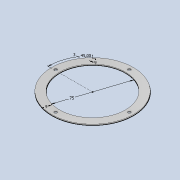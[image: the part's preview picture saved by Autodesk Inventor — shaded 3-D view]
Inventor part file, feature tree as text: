
AUTODESK INVENTOR PART (.ipt)
format: ipt  version: 2020.3 (Build 243373010, 373A)  size: 136,704 bytes
history: native  units: mm
features: sketch x2, extrude x2, hole x1, pattern_circular x1
ambient origin geometry x8: Origin, YZ Plane, XZ Plane, XY Plane, X Axis, Y Axis, Z Axis, Center Point
bodies: Solid1 (feature_tree)
feature tree (6):
  sketch  "Sketch2"  dims[d14=75.0mm d15=9.0mm]
  extrude  "Extrusion1"  Depth=9.0mm
  hole  "Hole1"  [1 undecoded]
  extrude  "Extrusion2"  Depth=0.25mm
  pattern_circular  "Circular Pattern1"  [2 undecoded]
  sketch  "Sketch3"  dims[d16=1.0mm d17=0.0mm d18=3.242mm d19=8.0mm d20=4.0mm d21=2.0mm d22=90.0deg d23=11.8mm d24=0.0mm d25=45.0deg d26=9.0mm d27=3.0mm d28=0.25mm d29=0.0mm d30=200.0mm d31=360.0deg]
note: 3 required parameter values undecoded (feature->parameter linkage not recoverable at this tier; creation-order binding heuristic only, values carry confidence <= 0.55)
